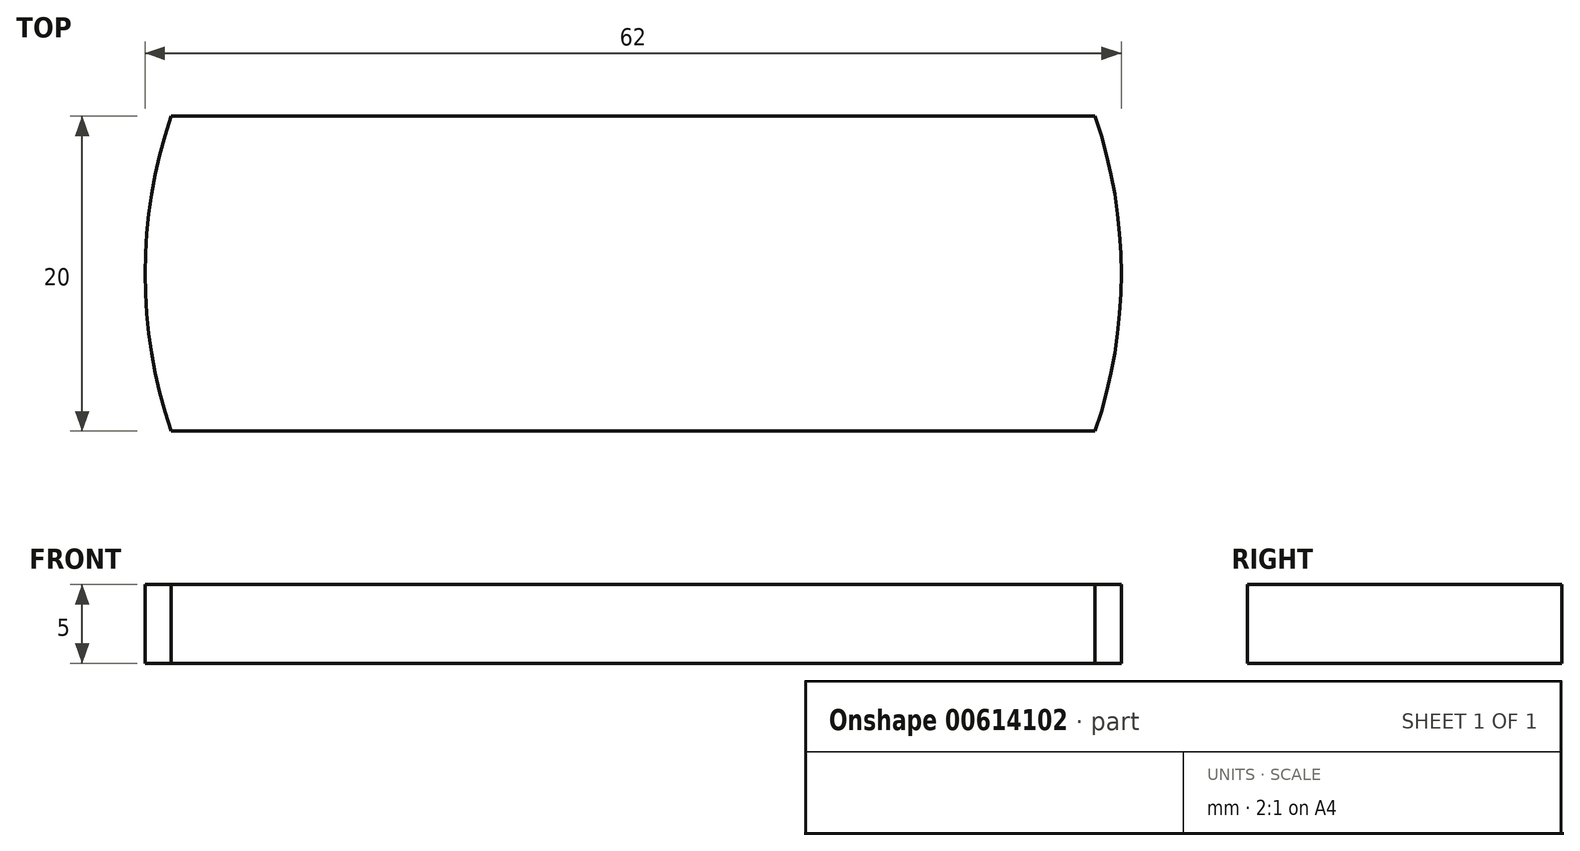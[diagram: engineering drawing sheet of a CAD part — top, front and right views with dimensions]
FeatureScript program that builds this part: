
annotation { "Feature Type Name" : "Feature", "Feature Type Description" : "" }
export const myFeature = defineFeature(function(context is Context, id is Id, definition is map)
    precondition{}
    {
        {
            var Q0;
            Q0=qCreatedBy(makeId("Top.planeOp"),FACE);
            var sketch = newSketch(context, id + "F0", { "sketchPlane" : qUnion([Q0])});
            skCircle(sketch, "E0", {"center": v(0, 0) * mm, "radius": 31 * mm});
            skLineSegment(sketch, "E1.bottom", {"start": v(42.81, 10) * mm, "end": v(-42.81, 10) * mm});
            skLineSegment(sketch, "E1.top", {"start": v(42.81, -10) * mm, "end": v(-42.81, -10) * mm});
            skLineSegment(sketch, "E1.left", {"start": v(42.81, 10) * mm, "end": v(42.81, -10) * mm});
            skLineSegment(sketch, "E1.right", {"start": v(-42.81, 10) * mm, "end": v(-42.81, -10) * mm});
            skSolve(sketch);
        }
        {
            var Q0;
            Q0=makeQuery(id+"F0.imprint","IMPRINT",FACE,{"disambiguationData":[TD([[makeQuery(id+"F0.imprint","IMPRINT",EDGE,{"derivedFrom":sQuery(id+"F0.wireOp",EDGE,"E0")}),1.0]])]});
            extrude(context, id + "F1", {"entities" : qUnion([Q0]), "depth" : 5 * mm, "offsetDistance" : 25 * mm});
        }
    });
